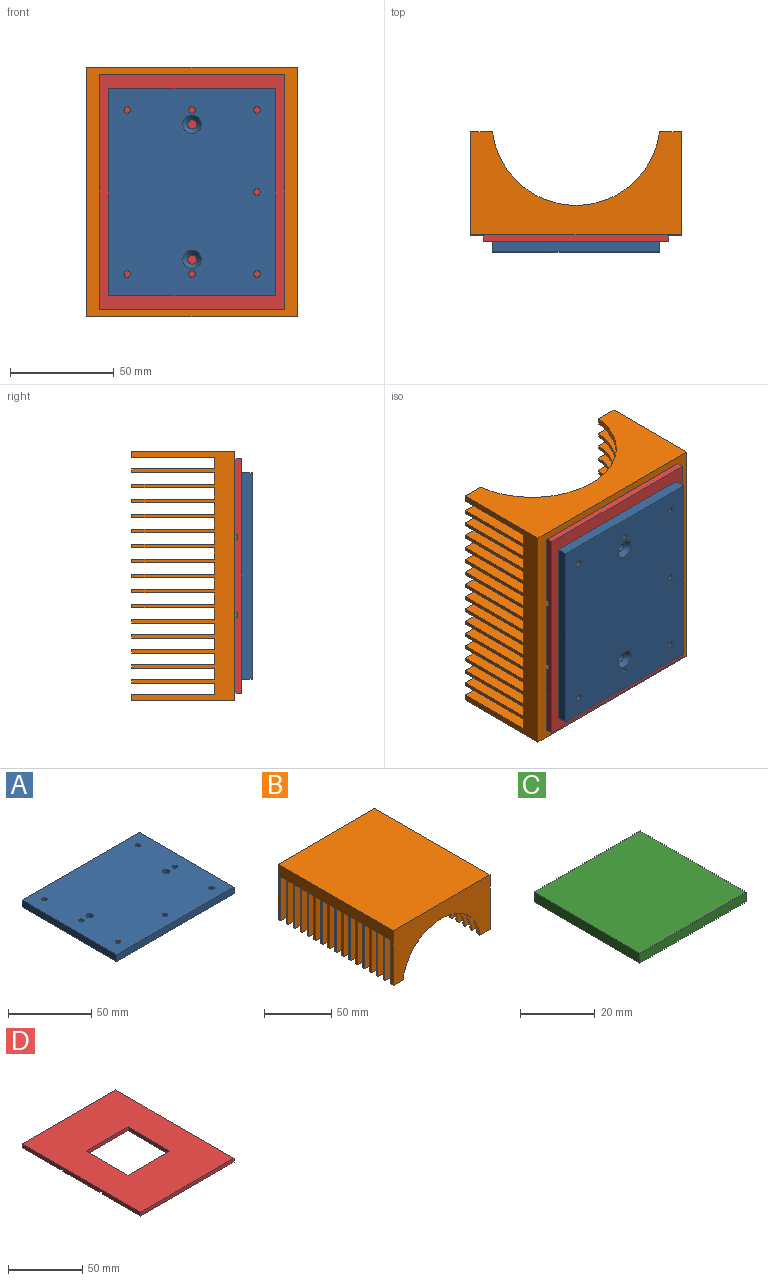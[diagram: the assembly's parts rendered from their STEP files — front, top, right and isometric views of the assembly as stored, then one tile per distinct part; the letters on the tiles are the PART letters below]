
ASSEMBLY  parts=4 mates=9
PART A: 17 faces, bbox 99.5x80.4x5.1 mm
  f0: plane 80.4x5.08mm, normal (-1,0,0), area 408.4mm2, adj f1,f3,f4,f5
  f1: plane 99.5x5.08mm, normal (0,-1,0), area 505.5mm2, adj f0,f2,f4,f5
  f2: plane 80.4x5.08mm, normal (1,0,0), area 408.4mm2, adj f1,f3,f4,f5
  f3: plane 99.5x5.08mm, normal (0,1,0), area 505.5mm2, adj f0,f2,f4,f5
  f4: plane 99.5x80.4mm, normal (0,0,1), area 7913.1mm2, adj f0,f1,f2,f3,f6,f8,f10,f11
  f5: plane 99.5x80.4mm, normal (0,0,-1), area 7817.4mm2, adj f0,f1,f2,f3,f7,f9,f10,f11
  f6: cylinder r=2.2mm len=4.4mm, axis (0,0,-1), area 38.7mm2, adj f4,f7
  f7: cone r=2.2mm half-angle=45deg, axis (0,0,-1), area 67.7mm2, adj f5,f6
  f8: cylinder r=2.2mm len=4.4mm, axis (0,0,-1), area 38.7mm2, adj f4,f9
  f9: cone r=2.2mm half-angle=45deg, axis (0,0,-1), area 67.7mm2, adj f5,f8
  f10: cylinder r=1.6mm len=5.08mm, axis (0,0,-1), area 51.1mm2, adj f4,f5
  f11: cylinder r=1.6mm len=5.08mm, axis (0,0,-1), area 51.1mm2, adj f4,f5
  f12: cylinder r=1.6mm len=5.08mm, axis (0,0,-1), area 51.1mm2, adj f4,f5
  f13: cylinder r=1.6mm len=5.08mm, axis (0,0,-1), area 51.1mm2, adj f4,f5
  f14: cylinder r=1.6mm len=5.08mm, axis (0,0,-1), area 51.1mm2, adj f4,f5
  f15: cylinder r=1.6mm len=5.08mm, axis (0,0,-1), area 51.1mm2, adj f4,f5
  f16: cylinder r=1.6mm len=5.08mm, axis (0,0,-1), area 51.1mm2, adj f4,f5
PART B: 104 faces, bbox 101.6x120.5x49.7 mm
  f0: plane 10.48x1.68mm, normal (0,0,-1), area 17.6mm2, adj f19,f84,f85,f87
  f1: plane 10.48x1.68mm, normal (0,0,-1), area 17.6mm2, adj f21,f23,f85,f103
  f2: plane 10.48x1.68mm, normal (0,0,-1), area 17.6mm2, adj f25,f27,f85,f102
  f3: plane 10.48x1.68mm, normal (0,0,-1), area 17.6mm2, adj f29,f31,f85,f101
  f4: plane 10.48x1.68mm, normal (0,0,-1), area 17.6mm2, adj f33,f35,f85,f100
  f5: plane 10.48x1.68mm, normal (0,0,-1), area 17.6mm2, adj f37,f39,f85,f99
  f6: plane 10.48x1.68mm, normal (0,0,-1), area 17.6mm2, adj f41,f43,f85,f98
  f7: plane 10.48x1.68mm, normal (0,0,-1), area 17.6mm2, adj f45,f47,f85,f97
  f8: plane 10.48x1.68mm, normal (0,0,-1), area 17.6mm2, adj f49,f51,f85,f96
  f9: plane 10.48x1.68mm, normal (0,0,-1), area 17.6mm2, adj f53,f55,f85,f95
  f10: plane 10.48x1.68mm, normal (0,0,-1), area 17.6mm2, adj f57,f59,f85,f94
  f11: plane 10.48x1.68mm, normal (0,0,-1), area 17.6mm2, adj f61,f63,f85,f93
  f12: plane 10.48x1.68mm, normal (0,0,-1), area 17.6mm2, adj f65,f67,f85,f92
  f13: plane 10.48x1.68mm, normal (0,0,-1), area 17.6mm2, adj f69,f71,f85,f91
  f14: plane 10.48x3.05mm, normal (0,0,-1), area 31.9mm2, adj f73,f75,f85,f90
  f15: plane 101.6x49.72mm, normal (0,-1,0), area 2869.1mm2, adj f16,f76,f77,f85,f86,f89
  f16: plane 10.48x2.92mm, normal (0,0,-1), area 30.6mm2, adj f15,f78,f86,f89
  f17: plane 10.48x1.68mm, normal (0,0,-1), area 17.6mm2, adj f80,f82,f85,f88
  f18: plane 10.48x1.68mm, normal (0,0,-1), area 17.6mm2, adj f19,f84,f86,f87
  f19: plane 101.6x39.81mm, normal (0,1,0), area 1862.6mm2, adj f0,f18,f20,f85,f86,f87
  f20: plane 101.6x5.59mm, normal (0,0,-1), area 567.7mm2, adj f19,f21,f85,f86
  f21: plane 101.6x39.81mm, normal (0,-1,0), area 1862.6mm2, adj f1,f20,f22,f85,f86,f103
  f22: plane 10.48x1.68mm, normal (0,0,-1), area 17.6mm2, adj f21,f23,f86,f103
  f23: plane 101.6x39.81mm, normal (0,1,0), area 1862.6mm2, adj f1,f22,f24,f85,f86,f103
  f24: plane 101.6x5.59mm, normal (0,0,-1), area 567.7mm2, adj f23,f25,f85,f86
  f25: plane 101.6x39.81mm, normal (0,-1,0), area 1862.6mm2, adj f2,f24,f26,f85,f86,f102
  f26: plane 10.48x1.68mm, normal (0,0,-1), area 17.6mm2, adj f25,f27,f86,f102
  f27: plane 101.6x39.81mm, normal (0,1,0), area 1862.6mm2, adj f2,f26,f28,f85,f86,f102
  f28: plane 101.6x5.59mm, normal (0,0,-1), area 567.7mm2, adj f27,f29,f85,f86
  f29: plane 101.6x39.81mm, normal (0,-1,0), area 1862.6mm2, adj f3,f28,f30,f85,f86,f101
  f30: plane 10.48x1.68mm, normal (0,0,-1), area 17.6mm2, adj f29,f31,f86,f101
  f31: plane 101.6x39.81mm, normal (0,1,0), area 1862.6mm2, adj f3,f30,f32,f85,f86,f101
  f32: plane 101.6x5.59mm, normal (0,0,-1), area 567.7mm2, adj f31,f33,f85,f86
  f33: plane 101.6x39.81mm, normal (0,-1,0), area 1862.6mm2, adj f4,f32,f34,f85,f86,f100
  f34: plane 10.48x1.68mm, normal (0,0,-1), area 17.6mm2, adj f33,f35,f86,f100
  f35: plane 101.6x39.81mm, normal (0,1,0), area 1862.6mm2, adj f4,f34,f36,f85,f86,f100
  f36: plane 101.6x5.59mm, normal (0,0,-1), area 567.7mm2, adj f35,f37,f85,f86
  f37: plane 101.6x39.81mm, normal (0,-1,0), area 1862.6mm2, adj f5,f36,f38,f85,f86,f99
  f38: plane 10.48x1.68mm, normal (0,0,-1), area 17.6mm2, adj f37,f39,f86,f99
  f39: plane 101.6x39.81mm, normal (0,1,0), area 1862.6mm2, adj f5,f38,f40,f85,f86,f99
  f40: plane 101.6x5.59mm, normal (0,0,-1), area 567.7mm2, adj f39,f41,f85,f86
  f41: plane 101.6x39.81mm, normal (0,-1,0), area 1862.6mm2, adj f6,f40,f42,f85,f86,f98
  f42: plane 10.48x1.68mm, normal (0,0,-1), area 17.6mm2, adj f41,f43,f86,f98
  f43: plane 101.6x39.81mm, normal (0,1,0), area 1862.6mm2, adj f6,f42,f44,f85,f86,f98
  f44: plane 101.6x5.59mm, normal (0,0,-1), area 567.7mm2, adj f43,f45,f85,f86
  f45: plane 101.6x39.81mm, normal (0,-1,0), area 1862.6mm2, adj f7,f44,f46,f85,f86,f97
  f46: plane 10.48x1.68mm, normal (0,0,-1), area 17.6mm2, adj f45,f47,f86,f97
  f47: plane 101.6x39.81mm, normal (0,1,0), area 1862.6mm2, adj f7,f46,f48,f85,f86,f97
  f48: plane 101.6x5.59mm, normal (0,0,-1), area 567.7mm2, adj f47,f49,f85,f86
  f49: plane 101.6x39.81mm, normal (0,-1,0), area 1862.6mm2, adj f8,f48,f50,f85,f86,f96
  f50: plane 10.48x1.68mm, normal (0,0,-1), area 17.6mm2, adj f49,f51,f86,f96
  f51: plane 101.6x39.81mm, normal (0,1,0), area 1862.6mm2, adj f8,f50,f52,f85,f86,f96
  f52: plane 101.6x5.59mm, normal (0,0,-1), area 567.7mm2, adj f51,f53,f85,f86
  f53: plane 101.6x39.81mm, normal (0,-1,0), area 1862.6mm2, adj f9,f52,f54,f85,f86,f95
  f54: plane 10.48x1.68mm, normal (0,0,-1), area 17.6mm2, adj f53,f55,f86,f95
  f55: plane 101.6x39.81mm, normal (0,1,0), area 1862.6mm2, adj f9,f54,f56,f85,f86,f95
  f56: plane 101.6x5.59mm, normal (0,0,-1), area 567.7mm2, adj f55,f57,f85,f86
  f57: plane 101.6x39.81mm, normal (0,-1,0), area 1862.6mm2, adj f10,f56,f58,f85,f86,f94
  f58: plane 10.48x1.68mm, normal (0,0,-1), area 17.6mm2, adj f57,f59,f86,f94
  f59: plane 101.6x39.81mm, normal (0,1,0), area 1862.6mm2, adj f10,f58,f60,f85,f86,f94
  f60: plane 101.6x5.59mm, normal (0,0,-1), area 567.7mm2, adj f59,f61,f85,f86
  f61: plane 101.6x39.81mm, normal (0,-1,0), area 1862.6mm2, adj f11,f60,f62,f85,f86,f93
  f62: plane 10.48x1.68mm, normal (0,0,-1), area 17.6mm2, adj f61,f63,f86,f93
  f63: plane 101.6x39.81mm, normal (0,1,0), area 1862.6mm2, adj f11,f62,f64,f85,f86,f93
  f64: plane 101.6x5.59mm, normal (0,0,-1), area 567.7mm2, adj f63,f65,f85,f86
  f65: plane 101.6x39.81mm, normal (0,-1,0), area 1862.6mm2, adj f12,f64,f66,f85,f86,f92
  f66: plane 10.48x1.68mm, normal (0,0,-1), area 17.6mm2, adj f65,f67,f86,f92
  f67: plane 101.6x39.81mm, normal (0,1,0), area 1862.6mm2, adj f12,f66,f68,f85,f86,f92
  f68: plane 101.6x5.59mm, normal (0,0,-1), area 567.7mm2, adj f67,f69,f85,f86
  f69: plane 101.6x39.81mm, normal (0,-1,0), area 1862.6mm2, adj f13,f68,f70,f85,f86,f91
  f70: plane 10.48x1.68mm, normal (0,0,-1), area 17.6mm2, adj f69,f71,f86,f91
  f71: plane 101.6x39.81mm, normal (0,1,0), area 1862.6mm2, adj f13,f70,f72,f85,f86,f91
  f72: plane 101.6x5.59mm, normal (0,0,-1), area 567.7mm2, adj f71,f73,f85,f86
  f73: plane 101.6x39.81mm, normal (0,-1,0), area 1862.6mm2, adj f14,f72,f74,f85,f86,f90
  f74: plane 10.48x3.05mm, normal (0,0,-1), area 31.9mm2, adj f73,f75,f86,f90
  f75: plane 101.6x49.72mm, normal (0,1,0), area 2869.1mm2, adj f14,f74,f76,f85,f86,f90
  f76: plane 120.52x101.6mm, normal (0,0,1), area 12245.1mm2, adj f15,f75,f85,f86
  f77: plane 10.48x2.92mm, normal (0,0,-1), area 30.6mm2, adj f15,f78,f85,f89
  f78: plane 101.6x39.81mm, normal (0,1,0), area 1862.6mm2, adj f16,f77,f79,f85,f86,f89
  f79: plane 101.6x5.59mm, normal (0,0,-1), area 567.7mm2, adj f78,f80,f85,f86
  f80: plane 101.6x39.81mm, normal (0,-1,0), area 1862.6mm2, adj f17,f79,f81,f85,f86,f88
  f81: plane 10.48x1.68mm, normal (0,0,-1), area 17.6mm2, adj f80,f82,f86,f88
  f82: plane 101.6x39.81mm, normal (0,1,0), area 1862.6mm2, adj f17,f81,f83,f85,f86,f88
  f83: plane 101.6x5.59mm, normal (0,0,-1), area 567.7mm2, adj f82,f84,f85,f86
  f84: plane 101.6x39.81mm, normal (0,-1,0), area 1862.6mm2, adj f0,f18,f83,f85,f86,f87
  f85: plane 120.52x49.72mm, normal (1,0,0), area 2432.7mm2, adj f0,f1,f2,f3,f4,f5,f6,f7
  f86: plane 120.52x49.72mm, normal (-1,0,0), area 2432.7mm2, adj f15,f16,f18,f19,f20,f21,f22,f23
  f87: cylinder r=40.64mm len=80.64mm, axis (0,-1,0), area 197mm2, adj f0,f18,f19,f84
  f88: cylinder r=40.64mm len=80.64mm, axis (0,-1,0), area 197mm2, adj f17,f80,f81,f82
  f89: cylinder r=40.64mm len=80.64mm, axis (0,-1,0), area 343.2mm2, adj f15,f16,f77,f78
  f90: cylinder r=40.64mm len=80.64mm, axis (0,-1,0), area 358.1mm2, adj f14,f73,f74,f75
  f91: cylinder r=40.64mm len=80.64mm, axis (0,-1,0), area 197mm2, adj f13,f69,f70,f71
  f92: cylinder r=40.64mm len=80.64mm, axis (0,-1,0), area 197mm2, adj f12,f65,f66,f67
  f93: cylinder r=40.64mm len=80.64mm, axis (0,-1,0), area 197mm2, adj f11,f61,f62,f63
  f94: cylinder r=40.64mm len=80.64mm, axis (0,-1,0), area 197mm2, adj f10,f57,f58,f59
  f95: cylinder r=40.64mm len=80.64mm, axis (0,-1,0), area 197mm2, adj f9,f53,f54,f55
  f96: cylinder r=40.64mm len=80.64mm, axis (0,-1,0), area 197mm2, adj f8,f49,f50,f51
  f97: cylinder r=40.64mm len=80.64mm, axis (0,-1,0), area 197mm2, adj f7,f45,f46,f47
  f98: cylinder r=40.64mm len=80.64mm, axis (0,-1,0), area 197mm2, adj f6,f41,f42,f43
  f99: cylinder r=40.64mm len=80.64mm, axis (0,-1,0), area 197mm2, adj f5,f37,f38,f39
  f100: cylinder r=40.64mm len=80.64mm, axis (0,-1,0), area 197mm2, adj f4,f33,f34,f35
  f101: cylinder r=40.64mm len=80.64mm, axis (0,-1,0), area 197mm2, adj f3,f29,f30,f31
  f102: cylinder r=40.64mm len=80.64mm, axis (0,-1,0), area 197mm2, adj f2,f25,f26,f27
  f103: cylinder r=40.64mm len=80.64mm, axis (0,-1,0), area 197mm2, adj f1,f21,f22,f23
PART C: 6 faces, bbox 40x40x3.2 mm
  f0: plane 40x3.18mm, normal (1,0,0), area 127mm2, adj f1,f3,f4,f5
  f1: plane 40x3.18mm, normal (0,1,0), area 127mm2, adj f0,f2,f4,f5
  f2: plane 40x3.18mm, normal (-1,0,0), area 127mm2, adj f1,f3,f4,f5
  f3: plane 40x3.18mm, normal (0,-1,0), area 127mm2, adj f0,f2,f4,f5
  f4: plane 40x40mm, normal (0,0,1), area 1600mm2, adj f0,f1,f2,f3
  f5: plane 40x40mm, normal (0,0,-1), area 1600mm2, adj f0,f1,f2,f3
PART D: 15 faces, bbox 89.3x113x3.2 mm
  f0: plane 113x89.3mm, normal (0,0,-1), area 7504.5mm2, adj f2,f4,f5,f6,f7,f8,f9
  f1: plane 34.93x24.65mm, normal (0,0,-1), area 860.8mm2, adj f2,f3,f11,f13
  f2: plane 113x3.18mm, normal (-1,0,0), area 352.3mm2, adj f0,f1,f4,f6,f8,f9,f10,f11
  f3: plane 40.01x3.18mm, normal (1,0,0), area 120.6mm2, adj f1,f4,f9,f10,f11,f12,f13,f14
  f4: plane 64.65x3.18mm, normal (0,-1,0), area 158.3mm2, adj f0,f2,f3,f5,f10,f12
  f5: plane 40.01x3.18mm, normal (-1,0,0), area 127mm2, adj f0,f4,f9,f10
  f6: plane 89.3x3.18mm, normal (0,-1,0), area 283.5mm2, adj f0,f2,f7,f10
  f7: plane 113x3.18mm, normal (1,0,0), area 358.8mm2, adj f0,f6,f8,f10
  f8: plane 89.3x3.18mm, normal (0,1,0), area 283.5mm2, adj f0,f2,f7,f10
  f9: plane 64.65x3.18mm, normal (0,1,0), area 158.3mm2, adj f0,f2,f3,f5,f10,f14
  f10: plane 113x89.3mm, normal (0,0,1), area 8490.5mm2, adj f2,f3,f4,f5,f6,f7,f8,f9
  f11: plane 24.65x1.27mm, normal (0,1,0), area 31.3mm2, adj f1,f2,f3,f12
  f12: plane 24.65x2.54mm, normal (0,0,-1), area 62.6mm2, adj f2,f3,f4,f11
  f13: plane 24.65x1.27mm, normal (0,-1,0), area 31.3mm2, adj f1,f2,f3,f14
  f14: plane 24.65x2.54mm, normal (0,0,-1), area 62.6mm2, adj f2,f3,f9,f13
PLACE A rot(axis=(-0.58,0.58,0.58),120deg) t=(0.69,-112.59,-26.89)mm
PLACE B rot(axis=(1,0,0),90deg) t=(-50.14,-104.33,-26.89)mm
PLACE C rot(axis=(1,0,0),90deg) t=(24.35,-104.33,-6.89)mm
PLACE D rot(axis=(1,0,0),90deg) t=(0.66,-104.33,-26.89)mm
MATE parallel B.f76 <-> A.f4  axis (0,-1,0) through (0.66,-104.33,-26.89)mm
MATE parallel C.f4 <-> B.f76  axis (0,-1,0) through (0.66,-107.51,-26.89)mm
MATE parallel A.f1 <-> B.f85  axis (1,0,0) through (40.89,-110.05,-26.89)mm
MATE fastened C.f4 <-> A.f4  axis (0,-1,0) through (0.66,-107.51,-26.89)mm
MATE planar D.f0 <-> B.f76  axis (0,1,0) through (4.91,-104.33,-26.89)mm
MATE fastened D.f10 <-> C.f4  axis (0,-1,0) through (0.66,-107.51,-26.89)mm
MATE planar A.f4 <-> C.f4  axis (0,1,0) through (0.66,-107.51,-26.89)mm
MATE planar C.f5 <-> B.f76  axis (0,1,0) through (0.66,-104.33,-26.89)mm
MATE fastened B.f76 <-> C.f5  axis (0,-1,0) through (0.66,-104.33,-26.89)mm
